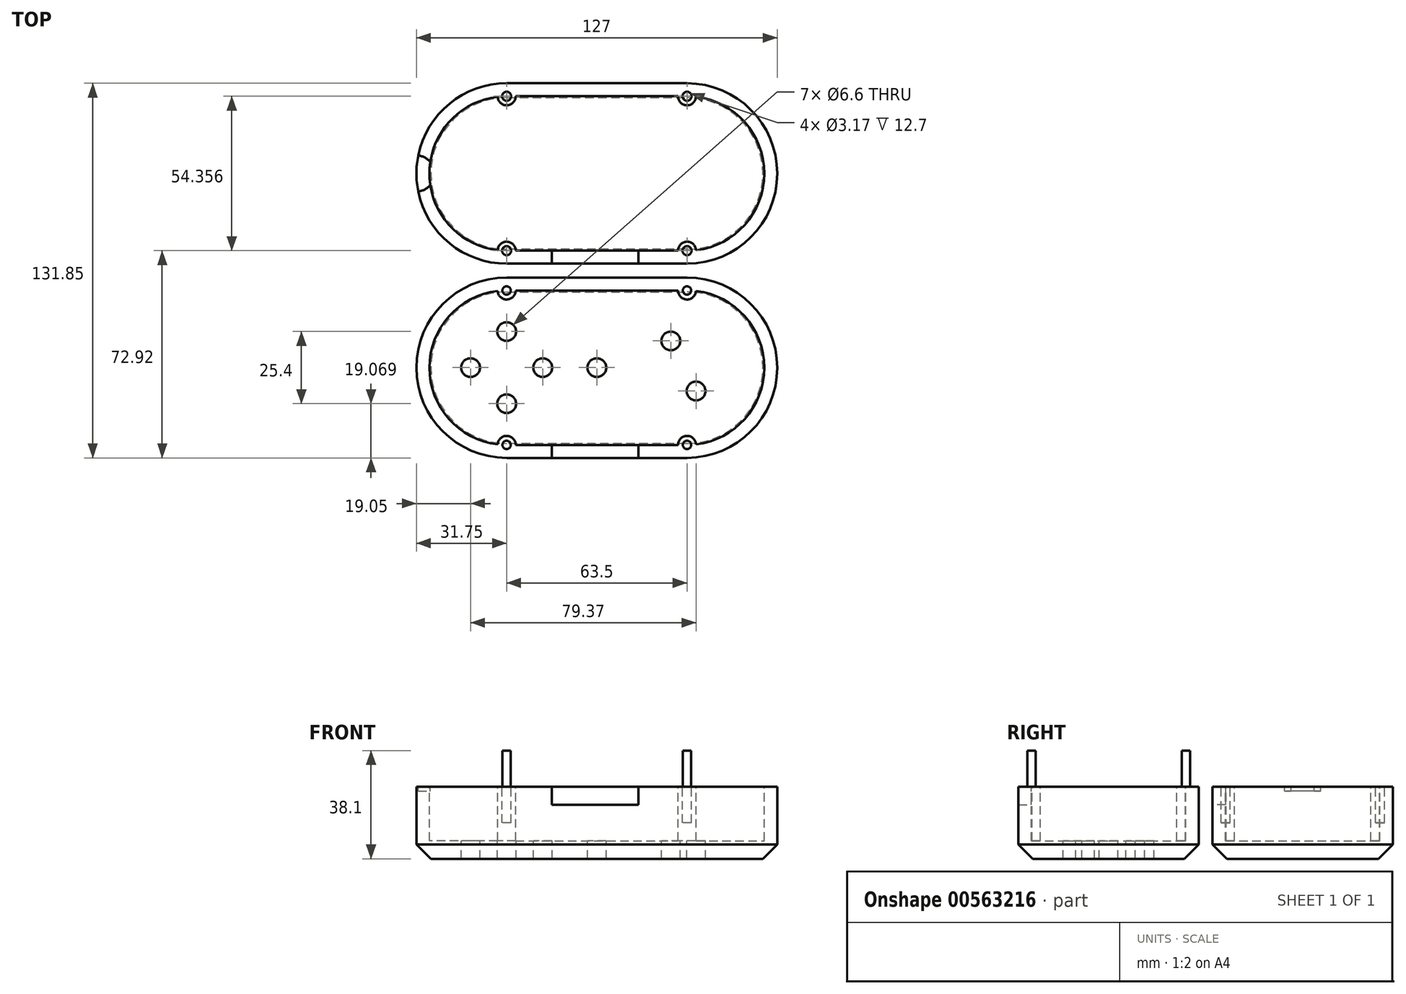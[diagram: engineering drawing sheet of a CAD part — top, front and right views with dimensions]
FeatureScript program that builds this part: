
annotation { "Feature Type Name" : "Feature", "Feature Type Description" : "" }
export const myFeature = defineFeature(function(context is Context, id is Id, definition is map)
    precondition{}
    {
        {
            var Q0;
            Q0=qCreatedBy(makeId("Top.planeOp"),FACE);
            var sketch = newSketch(context, id + "F0", { "sketchPlane" : qUnion([Q0])});
            skArc(sketch, "E0", {"start": v(0, 31.75) * mm, "mid": v(-31.75, 0) * mm, "end": v(0, -31.75) * mm});
            skArc(sketch, "E1", {"start": v(63.5, -31.75) * mm, "mid": v(95.25, 0) * mm, "end": v(63.5, 31.75) * mm});
            skLineSegment(sketch, "E2.bottom", {"start": v(0, 31.75) * mm, "end": v(63.5, 31.75) * mm});
            skLineSegment(sketch, "E2.top", {"start": v(0, -31.75) * mm, "end": v(63.5, -31.75) * mm});
            skArc(sketch, "E3", {"start": v(0, 100.1) * mm, "mid": v(-31.75, 68.35) * mm, "end": v(0, 36.6) * mm});
            skArc(sketch, "E4", {"start": v(63.5, 36.6) * mm, "mid": v(95.25, 68.35) * mm, "end": v(63.5, 100.1) * mm});
            skLineSegment(sketch, "E5.bottom", {"start": v(0, 100.1) * mm, "end": v(63.5, 100.1) * mm});
            skLineSegment(sketch, "E5.top", {"start": v(0, 36.6) * mm, "end": v(63.5, 36.6) * mm});
            skSolve(sketch);
        }
        {
            var Q0;
            Q0=makeQuery(id+"F0.imprint","IMPRINT",FACE,{"disambiguationData":[TD([[makeQuery(id+"F0.imprint","IMPRINT",EDGE,{"derivedFrom":sQuery(id+"F0.wireOp",EDGE,"E3")}),1.0]])]});
            var Q1;
            Q1=makeQuery(id+"F0.imprint","IMPRINT",FACE,{"disambiguationData":[TD([[makeQuery(id+"F0.imprint","IMPRINT",EDGE,{"derivedFrom":sQuery(id+"F0.wireOp",EDGE,"E0")}),1.0]])]});
            extrude(context, id + "F1", {"entities" : qUnion([Q0, Q1]), "depth" : 25.4 * mm, "offsetDistance" : 25.4 * mm});
        }
        {
            var Q0;
            Q0=makeQuery(id+"F1.opExtrude","CAP_FACE",FACE,{"disambiguationData":[OSD([sQuery(id+"F0.wireOp",EDGE,"E3"),sQuery(id+"F0.wireOp",EDGE,"E4"),sQuery(id+"F0.wireOp",EDGE,"E5.bottom"),sQuery(id+"F0.wireOp",EDGE,"E5.top")])],"isStart":false});
            var sketch = newSketch(context, id + "F2", { "sketchPlane" : qUnion([Q0])});
            skLineSegment(sketch, "E6.0", {"start": v(3.17, 95.53) * mm, "end": v(60.33, 95.53) * mm});
            skArc(sketch, "E6.1", {"start": v(-3.17, 95.34) * mm, "mid": v(-27.18, 68.35) * mm, "end": v(-3.17, 41.36) * mm});
            skLineSegment(sketch, "E6.2", {"start": v(3.17, 41.17) * mm, "end": v(60.33, 41.17) * mm});
            skArc(sketch, "E6.3", {"start": v(66.67, 41.36) * mm, "mid": v(90.68, 68.35) * mm, "end": v(66.67, 95.34) * mm});
            skArc(sketch, "E7", {"start": v(-3.17, 95.34) * mm, "mid": v(0.1, 92.35) * mm, "end": v(3.17, 95.53) * mm});
            skArc(sketch, "E8", {"start": v(3.17, 41.17) * mm, "mid": v(0.1, 44.34) * mm, "end": v(-3.17, 41.36) * mm});
            skArc(sketch, "E9", {"start": v(66.67, 41.36) * mm, "mid": v(63.4, 44.34) * mm, "end": v(60.33, 41.17) * mm});
            skArc(sketch, "E10", {"start": v(60.33, 95.53) * mm, "mid": v(63.4, 92.35) * mm, "end": v(66.67, 95.34) * mm});
            skSolve(sketch);
        }
        {
            var Q0;
            Q0=makeQuery(id+"F2.imprint","IMPRINT",FACE,{"disambiguationData":[TD([[makeQuery(id+"F2.imprint","IMPRINT",EDGE,{"derivedFrom":sQuery(id+"F2.wireOp",EDGE,"E6.0")}),-1.0]])]});
            extrude(context, id + "F3", {"entities" : qUnion([Q0]), "operationType" : NewBodyOperationType.REMOVE, "oppositeDirection" : true, "depth" : 19.05 * mm, "offsetDistance" : 25.4 * mm});
        }
        {
            var Q0;
            Q0=makeQuery(id+"F1.opExtrude","CAP_FACE",FACE,{"disambiguationData":[OSD([sQuery(id+"F0.wireOp",EDGE,"E0"),sQuery(id+"F0.wireOp",EDGE,"E1"),sQuery(id+"F0.wireOp",EDGE,"E2.bottom"),sQuery(id+"F0.wireOp",EDGE,"E2.top")])],"isStart":false});
            var sketch = newSketch(context, id + "F4", { "sketchPlane" : qUnion([Q0])});
            skLineSegment(sketch, "E11.0", {"start": v(3.17, 27.18) * mm, "end": v(60.33, 27.18) * mm});
            skArc(sketch, "E11.1", {"start": v(-3.17, 27) * mm, "mid": v(-27.18, 0) * mm, "end": v(-3.17, -27) * mm});
            skLineSegment(sketch, "E11.2", {"start": v(3.17, -27.18) * mm, "end": v(60.33, -27.18) * mm});
            skArc(sketch, "E11.3", {"start": v(66.67, -27) * mm, "mid": v(90.68, 0) * mm, "end": v(66.67, 27) * mm});
            skArc(sketch, "E12", {"start": v(-3.17, 27) * mm, "mid": v(0.1, 24) * mm, "end": v(3.17, 27.18) * mm});
            skArc(sketch, "E13", {"start": v(3.17, -27.18) * mm, "mid": v(0.1, -24) * mm, "end": v(-3.17, -27) * mm});
            skArc(sketch, "E14", {"start": v(66.67, -27) * mm, "mid": v(63.4, -24) * mm, "end": v(60.33, -27.18) * mm});
            skArc(sketch, "E15", {"start": v(60.33, 27.18) * mm, "mid": v(63.4, 24) * mm, "end": v(66.67, 27) * mm});
            skSolve(sketch);
        }
        {
            var Q0;
            Q0=makeQuery(id+"F4.imprint","IMPRINT",FACE,{"disambiguationData":[TD([[makeQuery(id+"F4.imprint","IMPRINT",EDGE,{"derivedFrom":sQuery(id+"F4.wireOp",EDGE,"E11.0")}),-1.0]])]});
            extrude(context, id + "F5", {"entities" : qUnion([Q0]), "operationType" : NewBodyOperationType.REMOVE, "oppositeDirection" : true, "depth" : 19.05 * mm, "offsetDistance" : 25.4 * mm});
        }
        {
            var Q0;
            Q0=makeQuery(id+"F1.opExtrude","CAP_FACE",FACE,{"disambiguationData":[OSD([sQuery(id+"F0.wireOp",EDGE,"E3"),sQuery(id+"F0.wireOp",EDGE,"E4"),sQuery(id+"F0.wireOp",EDGE,"E5.bottom"),sQuery(id+"F0.wireOp",EDGE,"E5.top")])],"isStart":false});
            var sketch = newSketch(context, id + "F6", { "sketchPlane" : qUnion([Q0])});
            skCircle(sketch, "E16", {"center": v(0, 95.53) * mm, "radius": 1.59 * mm});
            skCircle(sketch, "E17", {"center": v(0, 41.17) * mm, "radius": 1.59 * mm});
            skCircle(sketch, "E18", {"center": v(63.5, 41.17) * mm, "radius": 1.59 * mm});
            skCircle(sketch, "E19", {"center": v(63.5, 95.53) * mm, "radius": 1.59 * mm});
            skSolve(sketch);
        }
        {
            var Q0;
            Q0=makeQuery(id+"F6.imprint","IMPRINT",FACE,{"disambiguationData":[TD([[makeQuery(id+"F6.imprint","IMPRINT",EDGE,{"derivedFrom":sQuery(id+"F6.wireOp",EDGE,"E16")}),1.0]])]});
            var Q1;
            Q1=makeQuery(id+"F6.imprint","IMPRINT",FACE,{"disambiguationData":[TD([[makeQuery(id+"F6.imprint","IMPRINT",EDGE,{"derivedFrom":sQuery(id+"F6.wireOp",EDGE,"E17")}),1.0]])]});
            var Q2;
            Q2=makeQuery(id+"F6.imprint","IMPRINT",FACE,{"disambiguationData":[TD([[makeQuery(id+"F6.imprint","IMPRINT",EDGE,{"derivedFrom":sQuery(id+"F6.wireOp",EDGE,"E18")}),1.0]])]});
            var Q3;
            Q3=makeQuery(id+"F6.imprint","IMPRINT",FACE,{"disambiguationData":[TD([[makeQuery(id+"F6.imprint","IMPRINT",EDGE,{"derivedFrom":sQuery(id+"F6.wireOp",EDGE,"E19")}),1.0]])]});
            extrude(context, id + "F7", {"entities" : qUnion([Q0, Q1, Q2, Q3]), "operationType" : NewBodyOperationType.REMOVE, "oppositeDirection" : true, "depth" : 12.7 * mm, "offsetDistance" : 25.4 * mm});
        }
        {
            var Q0;
            Q0=makeQuery(id+"F1.opExtrude","CAP_FACE",FACE,{"disambiguationData":[OSD([sQuery(id+"F0.wireOp",EDGE,"E0"),sQuery(id+"F0.wireOp",EDGE,"E1"),sQuery(id+"F0.wireOp",EDGE,"E2.bottom"),sQuery(id+"F0.wireOp",EDGE,"E2.top")])],"isStart":false});
            var sketch = newSketch(context, id + "F8", { "sketchPlane" : qUnion([Q0])});
            skCircle(sketch, "E20", {"center": v(0, 27.18) * mm, "radius": 1.46 * mm});
            skCircle(sketch, "E21", {"center": v(0, -27.18) * mm, "radius": 1.46 * mm});
            skCircle(sketch, "E22", {"center": v(63.5, -27.18) * mm, "radius": 1.46 * mm});
            skCircle(sketch, "E23", {"center": v(63.5, 27.18) * mm, "radius": 1.46 * mm});
            skSolve(sketch);
        }
        {
            var Q0;
            Q0=makeQuery(id+"F8.imprint","IMPRINT",FACE,{"disambiguationData":[TD([[makeQuery(id+"F8.imprint","IMPRINT",EDGE,{"derivedFrom":sQuery(id+"F8.wireOp",EDGE,"E20")}),1.0]])]});
            var Q1;
            Q1=makeQuery(id+"F8.imprint","IMPRINT",FACE,{"disambiguationData":[TD([[makeQuery(id+"F8.imprint","IMPRINT",EDGE,{"derivedFrom":sQuery(id+"F8.wireOp",EDGE,"E21")}),1.0]])]});
            var Q2;
            Q2=makeQuery(id+"F8.imprint","IMPRINT",FACE,{"disambiguationData":[TD([[makeQuery(id+"F8.imprint","IMPRINT",EDGE,{"derivedFrom":sQuery(id+"F8.wireOp",EDGE,"E22")}),1.0]])]});
            var Q3;
            Q3=makeQuery(id+"F8.imprint","IMPRINT",FACE,{"disambiguationData":[TD([[makeQuery(id+"F8.imprint","IMPRINT",EDGE,{"derivedFrom":sQuery(id+"F8.wireOp",EDGE,"E23")}),1.0]])]});
            extrude(context, id + "F9", {"entities" : qUnion([Q0, Q1, Q2, Q3]), "operationType" : NewBodyOperationType.ADD, "depth" : 12.7 * mm, "offsetDistance" : 25.4 * mm});
        }
        {
            var Q0;
            Q0=makeQuery(id+"F5.boolean.opBoolean","COPY",FACE,{"derivedFrom":makeQuery(id+"F5.opExtrude","CAP_FACE",FACE,{"disambiguationData":[OSD([sQuery(id+"F4.wireOp",EDGE,"E11.0"),sQuery(id+"F4.wireOp",EDGE,"E11.1"),sQuery(id+"F4.wireOp",EDGE,"E11.2"),sQuery(id+"F4.wireOp",EDGE,"E11.3"),sQuery(id+"F4.wireOp",EDGE,"E12"),sQuery(id+"F4.wireOp",EDGE,"E13"),sQuery(id+"F4.wireOp",EDGE,"E14"),sQuery(id+"F4.wireOp",EDGE,"E15")])],"isStart":false})});
            var sketch = newSketch(context, id + "F10", { "sketchPlane" : qUnion([Q0])});
            skCircle(sketch, "E24", {"center": v(31.75, 0.02) * mm, "radius": 3.3 * mm});
            skPoint(sketch, "E25.center.orphan", {"position": v(51.83, 0) * mm});
            skPoint(sketch, "E26.center.orphan", {"position": v(74.79, 0) * mm});
            skCircle(sketch, "E27", {"center": v(57.8, 9.42) * mm, "radius": 3.3 * mm});
            skCircle(sketch, "E28", {"center": v(66.67, -8.22) * mm, "radius": 3.3 * mm});
            skPoint(sketch, "E29.center.orphan", {"position": v(-8.13, 2.03) * mm});
            skPoint(sketch, "E30.center.orphan", {"position": v(10.92, 2.03) * mm});
            skLineSegment(sketch, "E31", {"start": v(6.35, 0.02) * mm, "end": v(6.35, 0) * mm});
            skCircle(sketch, "E32", {"center": v(0, 12.72) * mm, "radius": 3.3 * mm});
            skCircle(sketch, "E33", {"center": v(0, -12.68) * mm, "radius": 3.3 * mm});
            skPoint(sketch, "E34.endSnap0", {"position": v(6.35, 0.02) * mm});
            skCircle(sketch, "E35", {"center": v(-12.7, 0.02) * mm, "radius": 3.3 * mm});
            skCircle(sketch, "E36", {"center": v(12.7, 0.02) * mm, "radius": 3.3 * mm});
            skPoint(sketch, "E37.orphan", {"position": v(-6.35, 12.72) * mm});
            skPoint(sketch, "E38.orphan", {"position": v(6.35, 12.72) * mm});
            skPoint(sketch, "E39.orphan", {"position": v(6.35, -12.68) * mm});
            skPoint(sketch, "E40.start.orphan", {"position": v(-6.35, -12.68) * mm});
            skPoint(sketch, "E41.orphan", {"position": v(-6.35, 0.02) * mm});
            skSolve(sketch);
        }
        {
            var Q0;
            Q0=makeQuery(id+"F10.imprint","IMPRINT",FACE,{"disambiguationData":[TD([[makeQuery(id+"F10.imprint","IMPRINT",EDGE,{"derivedFrom":sQuery(id+"F10.wireOp",EDGE,"E35")}),1.0]])]});
            var Q1;
            Q1=makeQuery(id+"F10.imprint","IMPRINT",FACE,{"disambiguationData":[TD([[makeQuery(id+"F10.imprint","IMPRINT",EDGE,{"derivedFrom":sQuery(id+"F10.wireOp",EDGE,"E33")}),1.0]])]});
            var Q2;
            Q2=makeQuery(id+"F10.imprint","IMPRINT",FACE,{"disambiguationData":[TD([[makeQuery(id+"F10.imprint","IMPRINT",EDGE,{"derivedFrom":sQuery(id+"F10.wireOp",EDGE,"E32")}),1.0]])]});
            var Q3;
            Q3=makeQuery(id+"F10.imprint","IMPRINT",FACE,{"disambiguationData":[TD([[makeQuery(id+"F10.imprint","IMPRINT",EDGE,{"derivedFrom":sQuery(id+"F10.wireOp",EDGE,"E36")}),1.0]])]});
            var Q4;
            Q4=makeQuery(id+"F10.imprint","IMPRINT",FACE,{"disambiguationData":[TD([[makeQuery(id+"F10.imprint","IMPRINT",EDGE,{"derivedFrom":sQuery(id+"F10.wireOp",EDGE,"E24")}),1.0]])]});
            var Q5;
            Q5=makeQuery(id+"F10.imprint","IMPRINT",FACE,{"disambiguationData":[TD([[makeQuery(id+"F10.imprint","IMPRINT",EDGE,{"derivedFrom":sQuery(id+"F10.wireOp",EDGE,"E28")}),1.0]])]});
            var Q6;
            Q6=makeQuery(id+"F10.imprint","IMPRINT",FACE,{"disambiguationData":[TD([[makeQuery(id+"F10.imprint","IMPRINT",EDGE,{"derivedFrom":sQuery(id+"F10.wireOp",EDGE,"E27")}),1.0]])]});
            extrude(context, id + "F11", {"entities" : qUnion([Q0, Q1, Q2, Q3, Q4, Q5, Q6]), "operationType" : NewBodyOperationType.REMOVE, "oppositeDirection" : true, "depth" : 25.4 * mm, "offsetDistance" : 25.4 * mm});
        }
        {
            var Q0;
            Q0=makeQuery(id+"F1.opExtrude","CAP_EDGE",EDGE,{"disambiguationData":[OSD([sQuery(id+"F0.wireOp",EDGE,"E0")])],"isStart":true});
            var Q1;
            Q1=makeQuery(id+"F1.opExtrude","CAP_EDGE",EDGE,{"disambiguationData":[OSD([sQuery(id+"F0.wireOp",EDGE,"E5.top")])],"isStart":true});
            chamfer(context, id + "F12", {"entities" : qUnion([Q0, Q1]), "width" : 5.08 * mm, "tangentPropagation" : true});
        }
        {
            var Q0;
            Q0=makeQuery(id+"F1.opExtrude","CAP_FACE",FACE,{"disambiguationData":[OSD([sQuery(id+"F0.wireOp",EDGE,"E0"),sQuery(id+"F0.wireOp",EDGE,"E1"),sQuery(id+"F0.wireOp",EDGE,"E2.bottom"),sQuery(id+"F0.wireOp",EDGE,"E2.top")])],"isStart":false});
            var sketch = newSketch(context, id + "F13", { "sketchPlane" : qUnion([Q0])});
            skLineSegment(sketch, "E42.bottom", {"start": v(46.36, -33.78) * mm, "end": v(15.88, -33.78) * mm});
            skPoint(sketch, "E42.middle", {"position": v(31.12, 31.75) * mm});
            skPoint(sketch, "E43.endSnap0", {"position": v(31.75, -27.18) * mm});
            skLineSegment(sketch, "E44", {"start": v(15.88, -33.78) * mm, "end": v(15.88, -25.3) * mm});
            skLineSegment(sketch, "E45", {"start": v(15.88, -25.3) * mm, "end": v(46.36, -25.3) * mm});
            skLineSegment(sketch, "E46", {"start": v(46.36, -33.78) * mm, "end": v(46.36, -25.3) * mm});
            skPoint(sketch, "E47.endSnap0", {"position": v(31.12, 33.88) * mm});
            skPoint(sketch, "E48.orphan", {"position": v(31.12, 114.02) * mm});
            skPoint(sketch, "E47.start.orphan", {"position": v(31.12, 25.4) * mm});
            skLineSegment(sketch, "E49", {"start": v(15.88, -25.3) * mm, "end": v(15.88, 119.46) * mm, "construction": true});
            skLineSegment(sketch, "E50", {"start": v(31.12, -25.3) * mm, "end": v(31.12, 114.02) * mm, "construction": true});
            skLineSegment(sketch, "E51", {"start": v(46.36, -25.3) * mm, "end": v(46.36, 114.02) * mm, "construction": true});
            skPoint(sketch, "E52.orphan", {"position": v(31.12, -33.78) * mm});
            skSolve(sketch);
        }
        {
            var Q0;
            {var subQ0=sQuery(id+"F13.wireOp",EDGE,"E45");Q0=makeQuery(id+"F13.imprint","IMPRINT",FACE,{"disambiguationData":[TD([[makeQuery(id+"F13.imprint","IMPRINT",EDGE,{"derivedFrom":subQ0}),-1.0]])]});}
            var Q1;
            {var subQ0=sQuery(id+"F13.wireOp",EDGE,"E44");var subQ1=makeQuery(id+"F1.opExtrude","CAP_EDGE",EDGE,{"disambiguationData":[OSD([sQuery(id+"F0.wireOp",EDGE,"E2.top")])],"isStart":false});var subQ2=makeQuery(id+"F13.imprint","INTERSECT",VERTEX,{"derivedFrom":[subQ1,subQ0]});Q1=makeQuery(id+"F13.imprint","IMPRINT",FACE,{"disambiguationData":[TD([[makeQuery(id+"F13.imprint","IMPRINT",EDGE,{"disambiguationData":[TD([[subQ2,-1.0]])],"derivedFrom":subQ0}),-1.0]])]});}
            var Q2;
            {var subQ0=sQuery(id+"F13.wireOp",EDGE,"E42.bottom");Q2=makeQuery(id+"F13.imprint","IMPRINT",FACE,{"disambiguationData":[TD([[makeQuery(id+"F13.imprint","IMPRINT",EDGE,{"derivedFrom":subQ0}),-1.0]])]});}
            extrude(context, id + "F14", {"entities" : qUnion([Q0, Q1, Q2]), "operationType" : NewBodyOperationType.REMOVE, "oppositeDirection" : true, "depth" : 6.35 * mm, "offsetDistance" : 25.4 * mm});
        }
        {
            var Q0;
            Q0=makeQuery(id+"F1.opExtrude","CAP_FACE",FACE,{"disambiguationData":[OSD([sQuery(id+"F0.wireOp",EDGE,"E3"),sQuery(id+"F0.wireOp",EDGE,"E4"),sQuery(id+"F0.wireOp",EDGE,"E5.bottom"),sQuery(id+"F0.wireOp",EDGE,"E5.top")])],"isStart":false});
            var sketch = newSketch(context, id + "F15", { "sketchPlane" : qUnion([Q0])});
            skLineSegment(sketch, "E53.bottom", {"start": v(15.88, 43.58) * mm, "end": v(46.35, 43.58) * mm});
            skLineSegment(sketch, "E53.top", {"start": v(15.88, 34.7) * mm, "end": v(46.35, 34.7) * mm});
            skLineSegment(sketch, "E53.left", {"start": v(15.88, 43.58) * mm, "end": v(15.88, 34.7) * mm});
            skLineSegment(sketch, "E53.right", {"start": v(46.35, 43.58) * mm, "end": v(46.35, 34.7) * mm});
            skSolve(sketch);
        }
        {
            var Q0;
            {var subQ0=sQuery(id+"F15.wireOp",EDGE,"E53.bottom");Q0=makeQuery(id+"F15.imprint","IMPRINT",FACE,{"disambiguationData":[TD([[makeQuery(id+"F15.imprint","IMPRINT",EDGE,{"derivedFrom":subQ0}),-1.0]])]});}
            var Q1;
            {var subQ0=sQuery(id+"F15.wireOp",EDGE,"E53.left");var subQ1=makeQuery(id+"F1.opExtrude","CAP_EDGE",EDGE,{"disambiguationData":[OSD([sQuery(id+"F0.wireOp",EDGE,"E5.top")])],"isStart":false});var subQ2=makeQuery(id+"F15.imprint","INTERSECT",VERTEX,{"derivedFrom":[subQ1,subQ0]});Q1=makeQuery(id+"F15.imprint","IMPRINT",FACE,{"disambiguationData":[TD([[makeQuery(id+"F15.imprint","IMPRINT",EDGE,{"disambiguationData":[TD([[subQ2,1.0]])],"derivedFrom":subQ0}),1.0]])]});}
            var Q2;
            {var subQ0=sQuery(id+"F15.wireOp",EDGE,"E53.top");Q2=makeQuery(id+"F15.imprint","IMPRINT",FACE,{"disambiguationData":[TD([[makeQuery(id+"F15.imprint","IMPRINT",EDGE,{"derivedFrom":subQ0}),1.0]])]});}
            extrude(context, id + "F16", {"entities" : qUnion([Q0, Q1, Q2]), "operationType" : NewBodyOperationType.REMOVE, "oppositeDirection" : true, "depth" : 6.35 * mm, "offsetDistance" : 25.4 * mm});
        }
        {
            var Q0;
            Q0=makeQuery(id+"F1.opExtrude","CAP_FACE",FACE,{"disambiguationData":[OSD([sQuery(id+"F0.wireOp",EDGE,"E3"),sQuery(id+"F0.wireOp",EDGE,"E4"),sQuery(id+"F0.wireOp",EDGE,"E5.bottom"),sQuery(id+"F0.wireOp",EDGE,"E5.top")])],"isStart":false});
            var sketch = newSketch(context, id + "F17", { "sketchPlane" : qUnion([Q0])});
            skCircle(sketch, "E54", {"center": v(95.25, 68.35) * mm, "radius": 6.35 * mm});
            skCircle(sketch, "E55", {"center": v(-31.75, 68.35) * mm, "radius": 6.35 * mm});
            skSolve(sketch);
        }
        {
            var Q0;
            {var subQ0=sQuery(id+"F17.wireOp",EDGE,"E55");var subQ1=makeQuery(id+"F1.opExtrude","CAP_EDGE",EDGE,{"disambiguationData":[OSD([sQuery(id+"F0.wireOp",EDGE,"E3")])],"isStart":false});var subQ2=makeQuery(id+"F17.imprint","INTERSECT",VERTEX,{"disambiguationData":[OD(0.0)],"derivedFrom":[subQ1,subQ0]});Q0=makeQuery(id+"F17.imprint","IMPRINT",FACE,{"disambiguationData":[TD([[makeQuery(id+"F17.imprint","IMPRINT",EDGE,{"disambiguationData":[TD([[subQ2,1.0]])],"derivedFrom":subQ0}),1.0]])]});}
            var Q1;
            {var subQ0=sQuery(id+"F17.wireOp",EDGE,"E55");var subQ1=makeQuery(id+"F3.boolean.opBoolean","COPY",EDGE,{"derivedFrom":makeQuery(id+"F3.opExtrude","CAP_EDGE",EDGE,{"disambiguationData":[OSD([sQuery(id+"F2.wireOp",EDGE,"E6.1")])],"isStart":true})});var subQ2=makeQuery(id+"F17.imprint","INTERSECT",VERTEX,{"disambiguationData":[OD(0.0)],"derivedFrom":[subQ1,subQ0]});Q1=makeQuery(id+"F17.imprint","IMPRINT",FACE,{"disambiguationData":[TD([[makeQuery(id+"F17.imprint","IMPRINT",EDGE,{"disambiguationData":[TD([[subQ2,1.0]])],"derivedFrom":subQ0}),1.0]])]});}
            var Q2;
            {var subQ0=sQuery(id+"F17.wireOp",EDGE,"E54");var subQ1=makeQuery(id+"F3.boolean.opBoolean","COPY",EDGE,{"derivedFrom":makeQuery(id+"F3.opExtrude","CAP_EDGE",EDGE,{"disambiguationData":[OSD([sQuery(id+"F2.wireOp",EDGE,"E6.3")])],"isStart":true})});var subQ2=makeQuery(id+"F17.imprint","INTERSECT",VERTEX,{"disambiguationData":[OD(0.0)],"derivedFrom":[subQ1,subQ0]});Q2=makeQuery(id+"F17.imprint","IMPRINT",FACE,{"disambiguationData":[TD([[makeQuery(id+"F17.imprint","IMPRINT",EDGE,{"disambiguationData":[TD([[subQ2,1.0]])],"derivedFrom":subQ0}),1.0]])]});}
            var Q3;
            {var subQ0=sQuery(id+"F17.wireOp",EDGE,"E54");var subQ1=makeQuery(id+"F3.boolean.opBoolean","COPY",EDGE,{"derivedFrom":makeQuery(id+"F3.opExtrude","CAP_EDGE",EDGE,{"disambiguationData":[OSD([sQuery(id+"F2.wireOp",EDGE,"E6.3")])],"isStart":true})});var subQ2=makeQuery(id+"F17.imprint","INTERSECT",VERTEX,{"disambiguationData":[OD(0.0)],"derivedFrom":[subQ1,subQ0]});Q3=makeQuery(id+"F17.imprint","IMPRINT",FACE,{"disambiguationData":[TD([[makeQuery(id+"F17.imprint","IMPRINT",EDGE,{"disambiguationData":[TD([[subQ2,-1.0]])],"derivedFrom":subQ0}),1.0]])]});}
            extrude(context, id + "F18", {"entities" : qUnion([Q0, Q1, Q2, Q3]), "operationType" : NewBodyOperationType.REMOVE, "oppositeDirection" : true, "depth" : 1.59 * mm, "offsetDistance" : 25.4 * mm});
        }
    });
